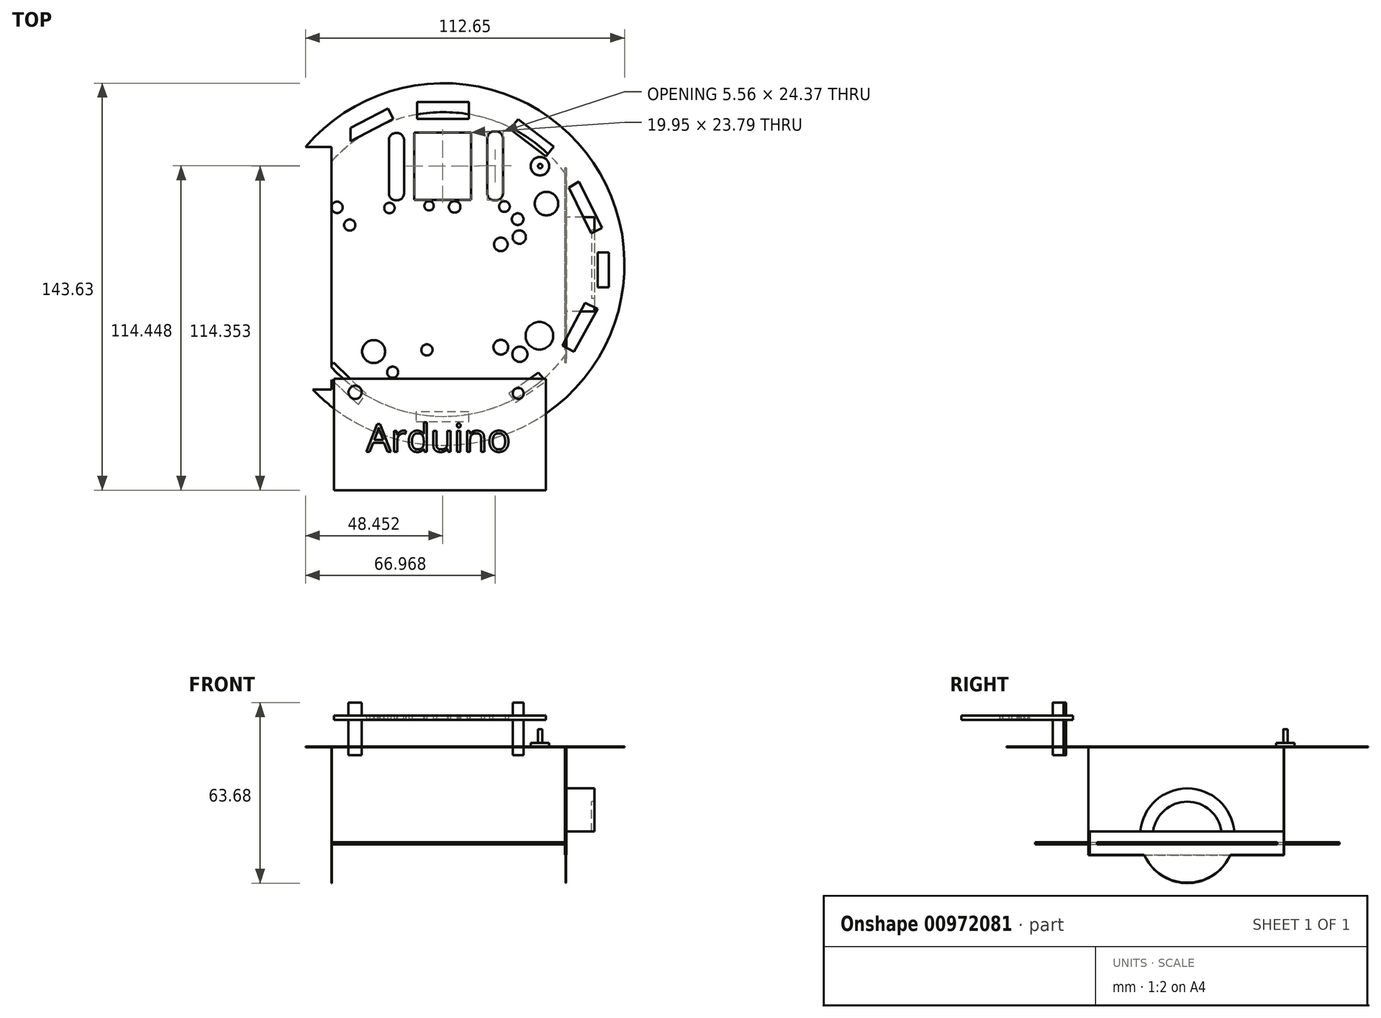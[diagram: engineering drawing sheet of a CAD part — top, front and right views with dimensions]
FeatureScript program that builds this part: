
annotation { "Feature Type Name" : "Feature", "Feature Type Description" : "" }
export const myFeature = defineFeature(function(context is Context, id is Id, definition is map)
    precondition{}
    {
        {
            var Q0;
            Q0=qCreatedBy(makeId("Top.planeOp"),FACE);
            var sketch = newSketch(context, id + "F0", { "sketchPlane" : qUnion([Q0])});
            skCircle(sketch, "E0", {"center": v(0, 0) * mm, "radius": 63.91 * mm});
            skSolve(sketch);
        }
        {
            var Q0;
            Q0 = qSketchRegion(id + "F0", true);
            extrude(context, id + "F1", {"entities" : qUnion([Q0]), "depth" : 0.25 * mm, "offsetDistance" : 25.4 * mm});
        }
        {
            var Q0;
            Q0=qCreatedBy(makeId("Top.planeOp"),FACE);
            var sketch = newSketch(context, id + "F2", { "sketchPlane" : qUnion([Q0])});
            skLineSegment(sketch, "E1", {"start": v(-9.3, 57.27) * mm, "end": v(8.92, 57.27) * mm});
            skLineSegment(sketch, "E2", {"start": v(26.38, 51.13) * mm, "end": v(38.88, 41.55) * mm});
            skLineSegment(sketch, "E3", {"start": v(47.87, 29.26) * mm, "end": v(55.93, 12.76) * mm});
            skLineSegment(sketch, "E4", {"start": v(58.42, 4.16) * mm, "end": v(58.42, -8.15) * mm});
            skLineSegment(sketch, "E5", {"start": v(54.45, -15.71) * mm, "end": v(46.1, -30.92) * mm});
            skLineSegment(sketch, "E6", {"start": v(36.2, -41.2) * mm, "end": v(25.4, -48.8) * mm});
            skLineSegment(sketch, "E7", {"start": v(8.92, -55.55) * mm, "end": v(-9.69, -55.55) * mm});
            skLineSegment(sketch, "E8", {"start": v(-30.03, -49.6) * mm, "end": v(-42.12, -38.28) * mm});
            skLineSegment(sketch, "E9", {"start": v(-48.98, -24.53) * mm, "end": v(-54.34, -11.89) * mm});
            skLineSegment(sketch, "E10", {"start": v(-57.66, -2.01) * mm, "end": v(-57.66, 9.38) * mm});
            skLineSegment(sketch, "E11", {"start": v(-54.34, 22.82) * mm, "end": v(-45, 40.2) * mm});
            skLineSegment(sketch, "E12", {"start": v(-32.8, 48.1) * mm, "end": v(-19.55, 55) * mm});
            skLineSegment(sketch, "E13.bottom", {"start": v(-10.27, 46.53) * mm, "end": v(9.69, 46.53) * mm});
            skLineSegment(sketch, "E13.top", {"start": v(-10.27, 22.74) * mm, "end": v(9.69, 22.74) * mm});
            skLineSegment(sketch, "E13.left", {"start": v(-10.27, 46.53) * mm, "end": v(-10.27, 22.74) * mm});
            skLineSegment(sketch, "E13.right", {"start": v(9.69, 46.53) * mm, "end": v(9.69, 22.74) * mm});
            skLineSegment(sketch, "E14", {"start": v(-19.55, 55) * mm, "end": v(-17.63, 51.32) * mm});
            skLineSegment(sketch, "E15", {"start": v(-17.63, 51.32) * mm, "end": v(-32.8, 43.42) * mm});
            skLineSegment(sketch, "E16", {"start": v(-32.8, 43.42) * mm, "end": v(-32.8, 48.1) * mm});
            skLineSegment(sketch, "E17", {"start": v(-9.3, 57.27) * mm, "end": v(-9.3, 51.32) * mm});
            skLineSegment(sketch, "E18", {"start": v(-9.3, 51.32) * mm, "end": v(8.92, 51.32) * mm});
            skLineSegment(sketch, "E19", {"start": v(8.92, 51.32) * mm, "end": v(8.92, 57.27) * mm});
            skLineSegment(sketch, "E20", {"start": v(-45, 40.2) * mm, "end": v(-42.77, 39) * mm});
            skLineSegment(sketch, "E21", {"start": v(-42.77, 39) * mm, "end": v(-51.52, 22.74) * mm});
            skLineSegment(sketch, "E22", {"start": v(-51.52, 22.74) * mm, "end": v(-54.34, 22.82) * mm});
            skLineSegment(sketch, "E23", {"start": v(-57.66, 9.38) * mm, "end": v(-54.34, 7.6) * mm});
            skLineSegment(sketch, "E24", {"start": v(-54.34, 7.6) * mm, "end": v(-54.34, -2.01) * mm});
            skLineSegment(sketch, "E25", {"start": v(-54.34, -2.01) * mm, "end": v(-57.66, -2.01) * mm});
            skLineSegment(sketch, "E26", {"start": v(-54.34, -11.89) * mm, "end": v(-51.52, -10.69) * mm});
            skLineSegment(sketch, "E27", {"start": v(-51.52, -10.69) * mm, "end": v(-46.27, -23.07) * mm});
            skLineSegment(sketch, "E28", {"start": v(-46.27, -23.07) * mm, "end": v(-48.98, -24.53) * mm});
            skLineSegment(sketch, "E29", {"start": v(-42.12, -38.28) * mm, "end": v(-38.8, -34.73) * mm});
            skLineSegment(sketch, "E30", {"start": v(-38.8, -34.73) * mm, "end": v(-27.41, -45.63) * mm});
            skLineSegment(sketch, "E31", {"start": v(-27.41, -45.63) * mm, "end": v(-30.03, -49.6) * mm});
            skLineSegment(sketch, "E32", {"start": v(-9.69, -55.55) * mm, "end": v(-9.69, -52.09) * mm});
            skLineSegment(sketch, "E33", {"start": v(-9.69, -52.09) * mm, "end": v(8.92, -52.09) * mm});
            skLineSegment(sketch, "E34", {"start": v(8.92, -52.09) * mm, "end": v(8.92, -55.55) * mm});
            skLineSegment(sketch, "E35", {"start": v(25.4, -48.8) * mm, "end": v(23.12, -45.55) * mm});
            skLineSegment(sketch, "E36", {"start": v(23.12, -45.55) * mm, "end": v(33.46, -38.28) * mm});
            skLineSegment(sketch, "E37", {"start": v(33.46, -38.28) * mm, "end": v(36.2, -41.2) * mm});
            skLineSegment(sketch, "E38", {"start": v(46.1, -30.92) * mm, "end": v(41.95, -28.7) * mm});
            skLineSegment(sketch, "E39", {"start": v(41.95, -28.7) * mm, "end": v(50.06, -13.6) * mm});
            skLineSegment(sketch, "E40", {"start": v(50.06, -13.6) * mm, "end": v(54.45, -15.71) * mm});
            skLineSegment(sketch, "E41", {"start": v(58.42, -8.15) * mm, "end": v(54.45, -8.15) * mm});
            skLineSegment(sketch, "E42", {"start": v(54.45, -8.15) * mm, "end": v(54.45, 4.16) * mm});
            skLineSegment(sketch, "E43", {"start": v(55.93, 12.76) * mm, "end": v(52.18, 10.93) * mm});
            skLineSegment(sketch, "E44", {"start": v(52.18, 10.93) * mm, "end": v(44.32, 27) * mm});
            skLineSegment(sketch, "E45", {"start": v(44.32, 27) * mm, "end": v(47.87, 29.26) * mm});
            skLineSegment(sketch, "E46", {"start": v(38.88, 41.55) * mm, "end": v(36.2, 38.05) * mm});
            skLineSegment(sketch, "E47", {"start": v(36.2, 38.05) * mm, "end": v(23.52, 47.77) * mm});
            skLineSegment(sketch, "E48", {"start": v(23.52, 47.77) * mm, "end": v(26.38, 51.13) * mm});
            skCircle(sketch, "E49", {"center": v(-5.08, 20.63) * mm, "radius": 1.65 * mm});
            skCircle(sketch, "E50", {"center": v(3.93, 20.24) * mm, "radius": 2.04 * mm});
            skLineSegment(sketch, "E51.bottom", {"start": v(-19.28, 46.34) * mm, "end": v(-13.91, 46.34) * mm});
            skLineSegment(sketch, "E51.top", {"start": v(-19.28, 22.54) * mm, "end": v(-13.91, 22.54) * mm});
            skLineSegment(sketch, "E51.left", {"start": v(-19.28, 46.34) * mm, "end": v(-19.28, 22.54) * mm});
            skLineSegment(sketch, "E51.right", {"start": v(-13.91, 46.34) * mm, "end": v(-13.91, 22.54) * mm});
            skLineSegment(sketch, "E52.bottom", {"start": v(15.45, 46.91) * mm, "end": v(21, 46.91) * mm});
            skLineSegment(sketch, "E52.top", {"start": v(15.45, 22.54) * mm, "end": v(21, 22.54) * mm});
            skLineSegment(sketch, "E52.left", {"start": v(15.45, 46.91) * mm, "end": v(15.45, 22.54) * mm});
            skLineSegment(sketch, "E52.right", {"start": v(21, 46.91) * mm, "end": v(21, 22.54) * mm});
            skCircle(sketch, "E53", {"center": v(-19.1, 19.86) * mm, "radius": 1.85 * mm});
            skCircle(sketch, "E54", {"center": v(21.51, 20.37) * mm, "radius": 1.88 * mm});
            skCircle(sketch, "E55", {"center": v(26.19, 15.92) * mm, "radius": 2.05 * mm});
            skCircle(sketch, "E56", {"center": v(26.76, 9.58) * mm, "radius": 2.34 * mm});
            skCircle(sketch, "E57", {"center": v(20.26, 7.02) * mm, "radius": 2.4 * mm});
            skCircle(sketch, "E58", {"center": v(-37.57, 20.08) * mm, "radius": 2 * mm});
            skCircle(sketch, "E59", {"center": v(-43.47, 28.5) * mm, "radius": 3.6 * mm});
            skCircle(sketch, "E60", {"center": v(-33.1, 13.84) * mm, "radius": 1.98 * mm});
            skLineSegment(sketch, "E61", {"start": v(54.45, 4.16) * mm, "end": v(58.42, 4.16) * mm});
            skCircle(sketch, "E62", {"center": v(-24.66, -30.8) * mm, "radius": 4.05 * mm});
            skCircle(sketch, "E63", {"center": v(-17.94, -38.09) * mm, "radius": 1.96 * mm});
            skCircle(sketch, "E64", {"center": v(-5.85, -30.22) * mm, "radius": 1.98 * mm});
            skCircle(sketch, "E65", {"center": v(33.87, -25.23) * mm, "radius": 4.88 * mm});
            skCircle(sketch, "E66", {"center": v(26.96, -31.75) * mm, "radius": 2.67 * mm});
            skCircle(sketch, "E67", {"center": v(20.24, -29.26) * mm, "radius": 2.58 * mm});
            skCircle(sketch, "E68", {"center": v(36.36, 21.4) * mm, "radius": 4.15 * mm});
            skSolve(sketch);
        }
        {
            var Q0;
            Q0 = qSketchRegion(id + "F2", true);
            extrude(context, id + "F3", {"entities" : qUnion([Q0]), "operationType" : NewBodyOperationType.REMOVE, "depth" : 53.34 * mm, "offsetDistance" : 25.4 * mm, "hasSecondDirection" : true, "secondDirectionOppositeDirection" : true, "secondDirectionDepth" : 76.45 * mm});
        }
        {
            var Q0;
            Q0=qCreatedBy(makeId("Top.planeOp"),FACE);
            var sketch = newSketch(context, id + "F4", { "sketchPlane" : qUnion([Q0])});
            skCircle(sketch, "E69", {"center": v(34.06, 34.63) * mm, "radius": 3.27 * mm});
            skSolve(sketch);
        }
        {
            var Q0;
            Q0 = qSketchRegion(id + "F4", true);
            extrude(context, id + "F5", {"entities" : qUnion([Q0]), "operationType" : NewBodyOperationType.ADD, "depth" : 1.52 * mm, "offsetDistance" : 25.4 * mm});
        }
        {
            var Q0;
            Q0=qCreatedBy(makeId("Top.planeOp"),FACE);
            var sketch = newSketch(context, id + "F6", { "sketchPlane" : qUnion([Q0])});
            skCircle(sketch, "E70", {"center": v(34.15, 34.65) * mm, "radius": 0.78 * mm});
            skSolve(sketch);
        }
        {
            var Q0;
            Q0 = qSketchRegion(id + "F6", true);
            extrude(context, id + "F7", {"entities" : qUnion([Q0]), "operationType" : NewBodyOperationType.ADD, "depth" : 6.35 * mm, "offsetDistance" : 25.4 * mm});
        }
        {
            var Q0;
            Q0=makeQuery(id+"F3.boolean.opBoolean","COPY",EDGE,{"derivedFrom":makeQuery(id+"F3.opExtrude","SWEPT_EDGE",EDGE,{"disambiguationData":[OSD([sQuery(id+"F2.wireOp",EDGE,"E52.bottom"),sQuery(id+"F2.wireOp",EDGE,"E52.left")])]})});
            var Q1;
            Q1=makeQuery(id+"F3.boolean.opBoolean","COPY",EDGE,{"derivedFrom":makeQuery(id+"F3.opExtrude","SWEPT_EDGE",EDGE,{"disambiguationData":[OSD([sQuery(id+"F2.wireOp",EDGE,"E52.bottom"),sQuery(id+"F2.wireOp",EDGE,"E52.right")])]})});
            var Q2;
            Q2=makeQuery(id+"F3.boolean.opBoolean","COPY",EDGE,{"derivedFrom":makeQuery(id+"F3.opExtrude","SWEPT_EDGE",EDGE,{"disambiguationData":[OSD([sQuery(id+"F2.wireOp",EDGE,"E52.top"),sQuery(id+"F2.wireOp",EDGE,"E52.right")])]})});
            var Q3;
            Q3=makeQuery(id+"F3.boolean.opBoolean","COPY",EDGE,{"derivedFrom":makeQuery(id+"F3.opExtrude","SWEPT_EDGE",EDGE,{"disambiguationData":[OSD([sQuery(id+"F2.wireOp",EDGE,"E52.top"),sQuery(id+"F2.wireOp",EDGE,"E52.left")])]})});
            var Q4;
            Q4=makeQuery(id+"F3.boolean.opBoolean","COPY",EDGE,{"derivedFrom":makeQuery(id+"F3.opExtrude","SWEPT_EDGE",EDGE,{"disambiguationData":[OSD([sQuery(id+"F2.wireOp",EDGE,"E51.bottom"),sQuery(id+"F2.wireOp",EDGE,"E51.left")])]})});
            var Q5;
            Q5=makeQuery(id+"F3.boolean.opBoolean","COPY",EDGE,{"derivedFrom":makeQuery(id+"F3.opExtrude","SWEPT_EDGE",EDGE,{"disambiguationData":[OSD([sQuery(id+"F2.wireOp",EDGE,"E51.bottom"),sQuery(id+"F2.wireOp",EDGE,"E51.right")])]})});
            var Q6;
            Q6=makeQuery(id+"F3.boolean.opBoolean","COPY",EDGE,{"derivedFrom":makeQuery(id+"F3.opExtrude","SWEPT_EDGE",EDGE,{"disambiguationData":[OSD([sQuery(id+"F2.wireOp",EDGE,"E51.top"),sQuery(id+"F2.wireOp",EDGE,"E51.left")])]})});
            var Q7;
            Q7=makeQuery(id+"F3.boolean.opBoolean","COPY",EDGE,{"derivedFrom":makeQuery(id+"F3.opExtrude","SWEPT_EDGE",EDGE,{"disambiguationData":[OSD([sQuery(id+"F2.wireOp",EDGE,"E51.top"),sQuery(id+"F2.wireOp",EDGE,"E51.right")])]})});
            fillet(context, id + "F8", {"entities" : qUnion([Q0, Q1, Q2, Q3, Q4, Q5, Q6, Q7]), "radius" : 2.54 * mm, "tangentPropagation" : true, "allowEdgeOverflow" : false});
        }
        {
            var Q0;
            Q0=qCreatedBy(makeId("Top.planeOp"),FACE);
            var sketch = newSketch(context, id + "F9", { "sketchPlane" : qUnion([Q0])});
            skCircle(sketch, "E71", {"center": v(-31.18, -45.19) * mm, "radius": 2.34 * mm});
            skCircle(sketch, "E72", {"center": v(26.38, -45.57) * mm, "radius": 1.93 * mm});
            skSolve(sketch);
        }
        {
            var Q0;
            Q0 = qSketchRegion(id + "F9", true);
            extrude(context, id + "F10", {"entities" : qUnion([Q0]), "operationType" : NewBodyOperationType.ADD, "depth" : 15.75 * mm, "offsetDistance" : 25.4 * mm, "hasSecondDirection" : true, "secondDirectionOppositeDirection" : true, "secondDirectionDepth" : 2.8 * mm});
        }
        {
            var Q0;
            Q0=qCreatedBy(makeId("Top.planeOp"),FACE);
            var sketch = newSketch(context, id + "F11", { "sketchPlane" : qUnion([Q0])});
            skLineSegment(sketch, "E73.bottom", {"start": v(-38.66, -40.39) * mm, "end": v(36.17, -40.39) * mm});
            skLineSegment(sketch, "E73.top", {"start": v(-38.66, -79.72) * mm, "end": v(36.17, -79.72) * mm});
            skLineSegment(sketch, "E73.left", {"start": v(-38.66, -40.39) * mm, "end": v(-38.66, -79.72) * mm});
            skLineSegment(sketch, "E73.right", {"start": v(36.17, -40.39) * mm, "end": v(36.17, -79.72) * mm});
            skSolve(sketch);
        }
        {
            var Q0;
            Q0 = qSketchRegion(id + "F11", true);
            extrude(context, id + "F12", {"entities" : qUnion([Q0]), "operationType" : NewBodyOperationType.ADD, "depth" : 11.18 * mm, "offsetDistance" : 25.4 * mm, "hasSecondDirection" : true, "secondDirectionOppositeDirection" : false, "secondDirectionDepth" : 9.65 * mm});
        }
        {
            var Q0;
            Q0=qCreatedBy(makeId("Top.planeOp"),FACE);
            var sketch = newSketch(context, id + "F13", { "sketchPlane" : qUnion([Q0])});
            skText(sketch, "E74", { "text": "Arduino", "fontName": "OpenSans-Regular.ttf"});
            const initialGuessF13  = {"E74": [-0.0272, -0.06613, 1, 0, 0.0098]};
            skSetInitialGuess(sketch, initialGuessF13);
            skSolve(sketch);
        }
        {
            var Q0;
            Q0 = qSketchRegion(id + "F13", true);
            extrude(context, id + "F14", {"entities" : qUnion([Q0]), "operationType" : NewBodyOperationType.REMOVE, "depth" : 20.57 * mm, "offsetDistance" : 25.4 * mm, "hasSecondDirection" : true, "secondDirectionOppositeDirection" : false, "secondDirectionDepth" : 9.9 * mm});
        }
        {
            var Q0;
            Q0=qCreatedBy(makeId("Right.planeOp"),FACE);
            var sketch = newSketch(context, id + "F15", { "sketchPlane" : qUnion([Q0])});
            skLineSegment(sketch, "E75.bottom", {"start": v(-34.86, 0) * mm, "end": v(34.02, 0) * mm});
            skLineSegment(sketch, "E75.top", {"start": v(-34.86, -37.9) * mm, "end": v(34.02, -37.9) * mm});
            skLineSegment(sketch, "E75.left", {"start": v(-34.86, 0) * mm, "end": v(-34.86, -37.9) * mm});
            skLineSegment(sketch, "E75.right", {"start": v(34.02, 0) * mm, "end": v(34.02, -37.9) * mm});
            skSolve(sketch);
        }
        {
            var Q0;
            Q0 = qSketchRegion(id + "F15", true);
            extrude(context, id + "F16", {"entities" : qUnion([Q0]), "operationType" : NewBodyOperationType.ADD, "depth" : 43.43 * mm, "offsetDistance" : 25.4 * mm, "hasSecondDirection" : true, "secondDirectionOppositeDirection" : false, "secondDirectionDepth" : 42.93 * mm});
        }
        {
            var Q0;
            Q0=qCreatedBy(makeId("Right.planeOp"),FACE);
            var sketch = newSketch(context, id + "F17", { "sketchPlane" : qUnion([Q0])});
            skLineSegment(sketch, "E76.bottom", {"start": v(-34.86, 0) * mm, "end": v(34.21, 0) * mm});
            skLineSegment(sketch, "E76.top", {"start": v(-34.86, -38.09) * mm, "end": v(34.21, -38.09) * mm});
            skLineSegment(sketch, "E76.left", {"start": v(-34.86, 0) * mm, "end": v(-34.86, -38.09) * mm});
            skLineSegment(sketch, "E76.right", {"start": v(34.21, 0) * mm, "end": v(34.21, -38.09) * mm});
            skSolve(sketch);
        }
        {
            var Q0;
            Q0 = qSketchRegion(id + "F17", true);
            extrude(context, id + "F18", {"entities" : qUnion([Q0]), "oppositeDirection" : true, "depth" : 39.62 * mm, "offsetDistance" : 25.4 * mm, "hasSecondDirection" : true, "secondDirectionOppositeDirection" : true, "secondDirectionDepth" : 39.37 * mm});
        }
        {
            var Q0;
            Q0=qCreatedBy(makeId("Right.planeOp"),FACE);
            var sketch = newSketch(context, id + "F19", { "sketchPlane" : qUnion([Q0])});
            skCircle(sketch, "E77", {"center": v(0, -31.18) * mm, "radius": 16.67 * mm});
            skSolve(sketch);
        }
        {
            var Q0;
            Q0 = qSketchRegion(id + "F19", true);
            extrude(context, id + "F20", {"entities" : qUnion([Q0]), "operationType" : NewBodyOperationType.ADD, "depth" : 53.34 * mm, "offsetDistance" : 25.4 * mm, "hasSecondDirection" : true, "secondDirectionOppositeDirection" : false, "secondDirectionDepth" : 43.18 * mm});
        }
        {
            var Q0;
            Q0=qCreatedBy(makeId("Right.planeOp"),FACE);
            var sketch = newSketch(context, id + "F21", { "sketchPlane" : qUnion([Q0])});
            skCircle(sketch, "E78", {"center": v(0, -31.37) * mm, "radius": 16.56 * mm});
            skSolve(sketch);
        }
        {
            var Q0;
            Q0 = qSketchRegion(id + "F21", true);
            extrude(context, id + "F22", {"entities" : qUnion([Q0]), "operationType" : NewBodyOperationType.ADD, "oppositeDirection" : true, "depth" : 47 * mm, "offsetDistance" : 25.4 * mm, "hasSecondDirection" : true, "secondDirectionOppositeDirection" : true, "secondDirectionDepth" : 39.45 * mm});
        }
        {
            var Q0;
            Q0=qCreatedBy(makeId("Right.planeOp"),FACE);
            var sketch = newSketch(context, id + "F23", { "sketchPlane" : qUnion([Q0])});
            skCircle(sketch, "E79", {"center": v(0, -31.37) * mm, "radius": 12.2 * mm});
            skSolve(sketch);
        }
        {
            var Q0;
            Q0 = qSketchRegion(id + "F23", true);
            extrude(context, id + "F24", {"entities" : qUnion([Q0]), "operationType" : NewBodyOperationType.REMOVE, "depth" : 104.14 * mm, "offsetDistance" : 25.4 * mm, "hasSecondDirection" : true, "secondDirectionOppositeDirection" : false, "secondDirectionDepth" : 52.32 * mm});
        }
        {
            var Q0;
            Q0=qCreatedBy(makeId("Right.planeOp"),FACE);
            var sketch = newSketch(context, id + "F25", { "sketchPlane" : qUnion([Q0])});
            skCircle(sketch, "E80", {"center": v(0, -31.18) * mm, "radius": 11.38 * mm});
            skSolve(sketch);
        }
        {
            var Q0;
            Q0 = qSketchRegion(id + "F25", true);
            extrude(context, id + "F26", {"entities" : qUnion([Q0]), "operationType" : NewBodyOperationType.REMOVE, "oppositeDirection" : true, "depth" : 58.17 * mm, "offsetDistance" : 25.4 * mm, "hasSecondDirection" : true, "secondDirectionOppositeDirection" : true, "secondDirectionDepth" : 44.96 * mm});
        }
        {
            var Q0;
            Q0=qCreatedBy(makeId("Top.planeOp"),FACE);
            var sketch = newSketch(context, id + "F27", { "sketchPlane" : qUnion([Q0])});
            skCircle(sketch, "E81", {"center": v(0, 0) * mm, "radius": 53.68 * mm});
            skSolve(sketch);
        }
        {
            var Q0;
            Q0 = qSketchRegion(id + "F27", true);
            extrude(context, id + "F28", {"entities" : qUnion([Q0]), "oppositeDirection" : true, "depth" : 34.3 * mm, "offsetDistance" : 25.4 * mm, "hasSecondDirection" : true, "secondDirectionOppositeDirection" : true, "secondDirectionDepth" : 33.53 * mm});
        }
        {
            var Q0;
            Q0=qCreatedBy(makeId("Top.planeOp"),FACE);
            var sketch = newSketch(context, id + "F29", { "sketchPlane" : qUnion([Q0])});
            skLineSegment(sketch, "E82", {"start": v(43.18, -34.42) * mm, "end": v(55.04, -34.42) * mm});
            skLineSegment(sketch, "E83", {"start": v(55.04, -34.42) * mm, "end": v(55.04, 34.79) * mm});
            skLineSegment(sketch, "E84", {"start": v(55.04, 34.79) * mm, "end": v(43.26, 34.79) * mm});
            skLineSegment(sketch, "E85", {"start": v(43.26, 34.79) * mm, "end": v(43.18, -34.42) * mm});
            skSolve(sketch);
        }
        {
            var Q0;
            Q0 = qSketchRegion(id + "F29", true);
            extrude(context, id + "F30", {"entities" : qUnion([Q0]), "operationType" : NewBodyOperationType.REMOVE, "oppositeDirection" : true, "depth" : 57.15 * mm, "offsetDistance" : 25.4 * mm, "hasSecondDirection" : true, "secondDirectionOppositeDirection" : true, "secondDirectionDepth" : 29.72 * mm});
        }
        {
            var Q0;
            Q0=qCreatedBy(makeId("Top.planeOp"),FACE);
            var sketch = newSketch(context, id + "F31", { "sketchPlane" : qUnion([Q0])});
            skLineSegment(sketch, "E86", {"start": v(-39.49, 41.34) * mm, "end": v(-67.17, 41.34) * mm});
            skLineSegment(sketch, "E87", {"start": v(-67.17, 41.34) * mm, "end": v(-67.17, -44.25) * mm});
            skLineSegment(sketch, "E88", {"start": v(-39.49, 41.34) * mm, "end": v(-39.49, -44.25) * mm});
            skLineSegment(sketch, "E89", {"start": v(-39.49, -44.25) * mm, "end": v(-67.17, -44.25) * mm});
            skSolve(sketch);
        }
        {
            var Q0;
            Q0 = qSketchRegion(id + "F31", true);
            extrude(context, id + "F32", {"entities" : qUnion([Q0]), "operationType" : NewBodyOperationType.REMOVE, "oppositeDirection" : true, "depth" : 57.66 * mm, "offsetDistance" : 25.4 * mm, "hasSecondDirection" : true, "secondDirectionOppositeDirection" : false, "secondDirectionDepth" : 47.24 * mm});
        }
    });
